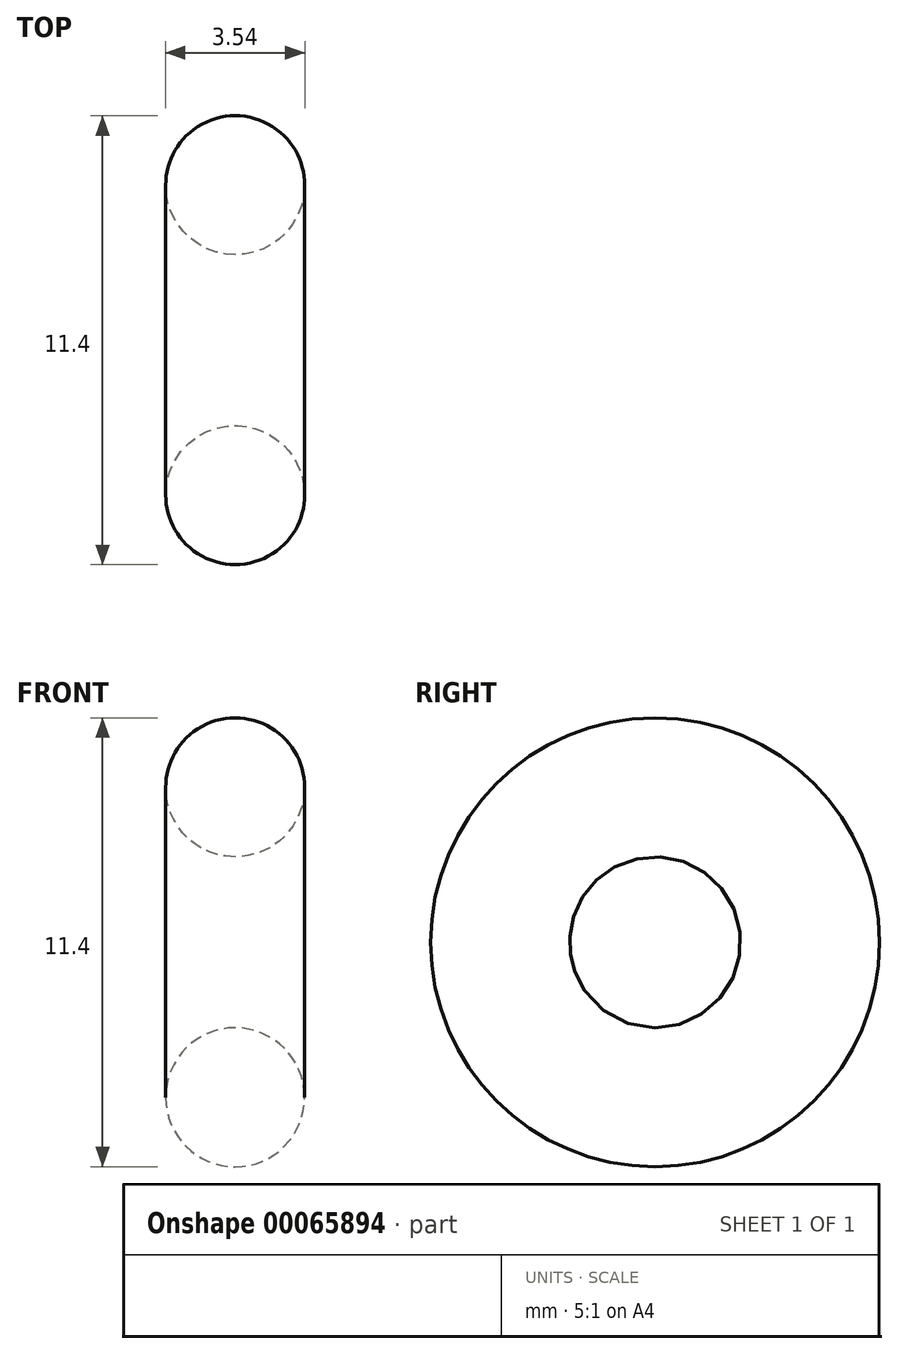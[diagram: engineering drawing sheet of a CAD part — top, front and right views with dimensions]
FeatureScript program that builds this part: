
annotation { "Feature Type Name" : "Feature", "Feature Type Description" : "" }
export const myFeature = defineFeature(function(context is Context, id is Id, definition is map)
    precondition{}
    {
        {
            var Q0;
            Q0=qCreatedBy(makeId("Front.planeOp"),FACE);
            var sketch = newSketch(context, id + "F0", { "sketchPlane" : qUnion([Q0])});
            skLineSegment(sketch, "E0", {"start": v(0, 0) * mm, "end": v(-6.06, 0) * mm, "construction": true});
            skCircle(sketch, "E1", {"center": v(0, 3.94) * mm, "radius": 1.77 * mm});
            skSolve(sketch);
        }
        {
            var Q0;
            Q0=makeQuery(id+"F0.imprint","IMPRINT",FACE,{"disambiguationData":[TD([[makeQuery(id+"F0.imprint","IMPRINT",EDGE,{"derivedFrom":sQuery(id+"F0.wireOp",EDGE,"E1")}),1.0]])]});
            var Q1;
            Q1=sQuery(id+"F0.wireOp",EDGE,"E0");
            revolve(context, id + "F1", {"entities" : qUnion([Q0]), "axis" : qUnion([Q1]), "revolveType" : RevolveType.FULL});
        }
    });
